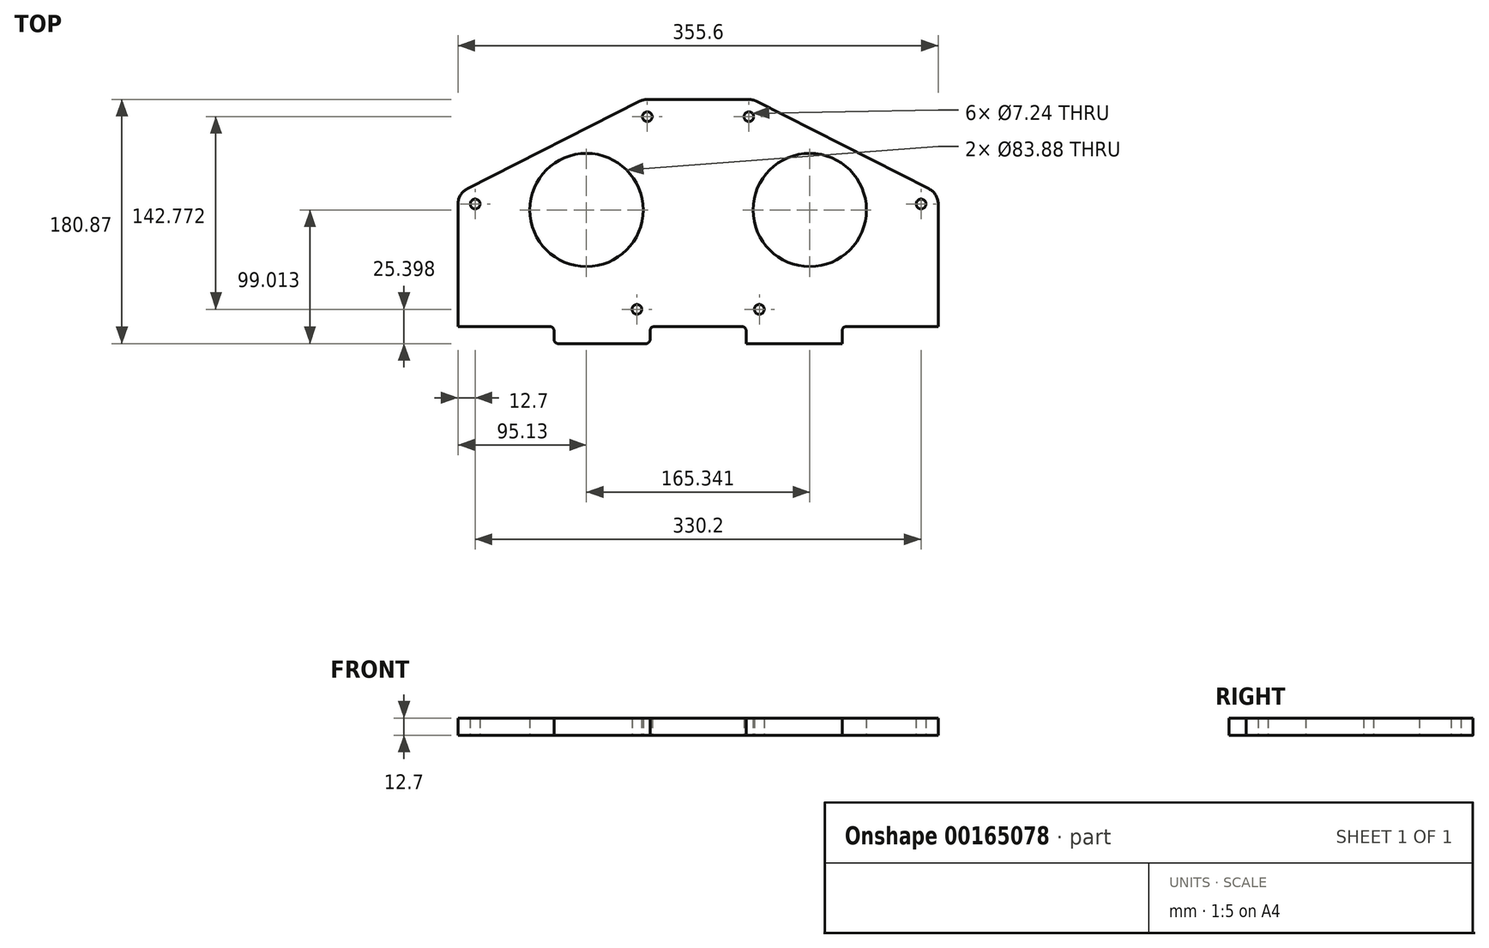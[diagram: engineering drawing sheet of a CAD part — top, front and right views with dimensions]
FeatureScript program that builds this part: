
annotation { "Feature Type Name" : "Feature", "Feature Type Description" : "" }
export const myFeature = defineFeature(function(context is Context, id is Id, definition is map)
    precondition{}
    {
        {
            var Q0;
            Q0=qCreatedBy(makeId("Top.planeOp"),FACE);
            var sketch = newSketch(context, id + "F0", { "sketchPlane" : qUnion([Q0])});
            skLineSegment(sketch, "E0.bottom", {"start": v(-37.6, 0) * mm, "end": v(37.6, 0) * mm});
            skLineSegment(sketch, "E0.top", {"start": v(-177.8, -180.87) * mm, "end": v(177.8, -180.87) * mm});
            skLineSegment(sketch, "E0.left", {"start": v(-177.8, -77.4) * mm, "end": v(-177.8, -180.87) * mm});
            skLineSegment(sketch, "E0.right", {"start": v(177.8, -77.4) * mm, "end": v(177.8, -180.87) * mm});
            skLineSegment(sketch, "E1", {"start": v(-177.8, -81.86) * mm, "end": v(-82.67, -81.86) * mm, "construction": true});
            skLineSegment(sketch, "E2", {"start": v(-82.67, -81.86) * mm, "end": v(-82.67, 0) * mm, "construction": true});
            skLineSegment(sketch, "E3", {"start": v(177.8, -81.86) * mm, "end": v(82.67, -81.86) * mm, "construction": true});
            skLineSegment(sketch, "E4", {"start": v(82.67, -81.86) * mm, "end": v(82.67, 0) * mm, "construction": true});
            skCircle(sketch, "E5", {"center": v(-82.67, -81.86) * mm, "radius": 41.94 * mm});
            skCircle(sketch, "E6", {"center": v(82.67, -81.86) * mm, "radius": 41.94 * mm});
            skLineSegment(sketch, "E7", {"start": v(-82.67, -81.86) * mm, "end": v(-45.32, -155.47) * mm, "construction": true});
            skLineSegment(sketch, "E8", {"start": v(-45.32, -155.47) * mm, "end": v(-165.1, -77.4) * mm, "construction": true});
            skLineSegment(sketch, "E9", {"start": v(-165.1, -77.4) * mm, "end": v(-82.67, -81.86) * mm, "construction": true});
            skLineSegment(sketch, "E10", {"start": v(-82.67, -81.86) * mm, "end": v(-37.6, -12.7) * mm, "construction": true});
            skLineSegment(sketch, "E11", {"start": v(-37.6, -12.7) * mm, "end": v(-165.1, -77.4) * mm, "construction": true});
            skLineSegment(sketch, "E12", {"start": v(-45.32, -155.47) * mm, "end": v(-37.6, -12.7) * mm, "construction": true});
            skLineSegment(sketch, "E13", {"start": v(82.67, -81.86) * mm, "end": v(165.1, -77.4) * mm, "construction": true});
            skLineSegment(sketch, "E14", {"start": v(165.1, -77.4) * mm, "end": v(45.32, -155.47) * mm, "construction": true});
            skLineSegment(sketch, "E15", {"start": v(45.32, -155.47) * mm, "end": v(82.67, -81.86) * mm, "construction": true});
            skLineSegment(sketch, "E16", {"start": v(82.67, -81.86) * mm, "end": v(37.6, -12.7) * mm, "construction": true});
            skLineSegment(sketch, "E17", {"start": v(37.6, -12.7) * mm, "end": v(45.32, -155.47) * mm, "construction": true});
            skLineSegment(sketch, "E18", {"start": v(37.6, -12.7) * mm, "end": v(165.1, -77.4) * mm, "construction": true});
            skCircle(sketch, "E19", {"center": v(-45.32, -155.47) * mm, "radius": 3.62 * mm});
            skCircle(sketch, "E20", {"center": v(-37.6, -12.7) * mm, "radius": 3.62 * mm});
            skCircle(sketch, "E21", {"center": v(-165.1, -77.4) * mm, "radius": 3.62 * mm});
            skCircle(sketch, "E22", {"center": v(45.32, -155.47) * mm, "radius": 3.62 * mm});
            skCircle(sketch, "E23", {"center": v(165.1, -77.4) * mm, "radius": 3.62 * mm});
            skCircle(sketch, "E24", {"center": v(37.6, -12.7) * mm, "radius": 3.62 * mm});
            skLineSegment(sketch, "E25", {"start": v(45.32, -155.47) * mm, "end": v(-45.32, -155.47) * mm, "construction": true});
            skLineSegment(sketch, "E26", {"start": v(0, -155.47) * mm, "end": v(0, -180.87) * mm, "construction": true});
            skArc(sketch, "E27", {"start": v(43.34, -1.37) * mm, "mid": v(40.55, -0.35) * mm, "end": v(37.6, 0) * mm});
            skArc(sketch, "E28", {"start": v(177.8, -77.4) * mm, "mid": v(175.92, -70.75) * mm, "end": v(170.85, -66.07) * mm});
            skLineSegment(sketch, "E29", {"start": v(170.85, -66.07) * mm, "end": v(43.34, -1.37) * mm});
            skArc(sketch, "E30", {"start": v(-37.6, 0) * mm, "mid": v(-40.55, -0.35) * mm, "end": v(-43.34, -1.37) * mm});
            skArc(sketch, "E31", {"start": v(-170.85, -66.07) * mm, "mid": v(-175.92, -70.75) * mm, "end": v(-177.8, -77.4) * mm});
            skLineSegment(sketch, "E32", {"start": v(-43.34, -1.37) * mm, "end": v(-170.85, -66.07) * mm});
            skSolve(sketch);
        }
        {
            var Q0;
            Q0=makeQuery(id+"F0.imprint","IMPRINT",FACE,{"disambiguationData":[TD([[makeQuery(id+"F0.imprint","IMPRINT",EDGE,{"derivedFrom":sQuery(id+"F0.wireOp",EDGE,"E0.top")}),1.0]])]});
            extrude(context, id + "F1", {"entities" : qUnion([Q0]), "depth" : 12.7 * mm});
        }
        {
            var Q0;
            Q0=makeQuery(id+"F1.opExtrude","CAP_FACE",FACE,{"disambiguationData":[OSD([sQuery(id+"F0.wireOp",EDGE,"E0.bottom"),sQuery(id+"F0.wireOp",EDGE,"E0.top"),sQuery(id+"F0.wireOp",EDGE,"E0.left"),sQuery(id+"F0.wireOp",EDGE,"E0.right"),sQuery(id+"F0.wireOp",EDGE,"E5"),sQuery(id+"F0.wireOp",EDGE,"E6"),sQuery(id+"F0.wireOp",EDGE,"E19"),sQuery(id+"F0.wireOp",EDGE,"E20"),sQuery(id+"F0.wireOp",EDGE,"E21"),sQuery(id+"F0.wireOp",EDGE,"E22"),sQuery(id+"F0.wireOp",EDGE,"E23"),sQuery(id+"F0.wireOp",EDGE,"E24"),sQuery(id+"F0.wireOp",EDGE,"E27"),sQuery(id+"F0.wireOp",EDGE,"E28"),sQuery(id+"F0.wireOp",EDGE,"E29"),sQuery(id+"F0.wireOp",EDGE,"E30"),sQuery(id+"F0.wireOp",EDGE,"E31"),sQuery(id+"F0.wireOp",EDGE,"E32")])],"isStart":false});
            var sketch = newSketch(context, id + "F2", { "sketchPlane" : qUnion([Q0])});
            skLineSegment(sketch, "E33.bottom", {"start": v(-177.8, -180.87) * mm, "end": v(-106.68, -180.87) * mm});
            skLineSegment(sketch, "E33.top", {"start": v(-177.8, -168.17) * mm, "end": v(-106.68, -168.17) * mm});
            skLineSegment(sketch, "E33.left", {"start": v(-177.8, -180.87) * mm, "end": v(-177.8, -168.17) * mm});
            skLineSegment(sketch, "E33.right", {"start": v(-106.68, -180.87) * mm, "end": v(-106.68, -168.17) * mm});
            skLineSegment(sketch, "E34.bottom", {"start": v(106.68, -180.87) * mm, "end": v(177.8, -180.87) * mm});
            skLineSegment(sketch, "E34.top", {"start": v(106.68, -168.17) * mm, "end": v(177.8, -168.17) * mm});
            skLineSegment(sketch, "E34.left", {"start": v(106.68, -180.87) * mm, "end": v(106.68, -168.17) * mm});
            skLineSegment(sketch, "E34.right", {"start": v(177.8, -180.87) * mm, "end": v(177.8, -168.17) * mm});
            skLineSegment(sketch, "E35.bottom", {"start": v(-35.56, -180.87) * mm, "end": v(35.56, -180.87) * mm});
            skLineSegment(sketch, "E35.top", {"start": v(-35.56, -168.17) * mm, "end": v(35.56, -168.17) * mm});
            skLineSegment(sketch, "E35.left", {"start": v(-35.56, -180.87) * mm, "end": v(-35.56, -168.17) * mm});
            skLineSegment(sketch, "E35.right", {"start": v(35.56, -180.87) * mm, "end": v(35.56, -168.17) * mm});
            skLineSegment(sketch, "E36", {"start": v(-106.68, -168.17) * mm, "end": v(-35.56, -168.17) * mm, "construction": true});
            skLineSegment(sketch, "E37", {"start": v(106.68, -168.17) * mm, "end": v(35.56, -168.17) * mm, "construction": true});
            skSolve(sketch);
        }
        {
            var Q0;
            Q0 = qSketchRegion(id + "F2", true);
            var Q1;
            Q1=makeQuery(id+"F1.opExtrude","CAP_FACE",FACE,{"disambiguationData":[OSD([sQuery(id+"F0.wireOp",EDGE,"E0.bottom"),sQuery(id+"F0.wireOp",EDGE,"E0.top"),sQuery(id+"F0.wireOp",EDGE,"E0.left"),sQuery(id+"F0.wireOp",EDGE,"E0.right"),sQuery(id+"F0.wireOp",EDGE,"E5"),sQuery(id+"F0.wireOp",EDGE,"E6"),sQuery(id+"F0.wireOp",EDGE,"E19"),sQuery(id+"F0.wireOp",EDGE,"E20"),sQuery(id+"F0.wireOp",EDGE,"E21"),sQuery(id+"F0.wireOp",EDGE,"E22"),sQuery(id+"F0.wireOp",EDGE,"E23"),sQuery(id+"F0.wireOp",EDGE,"E24"),sQuery(id+"F0.wireOp",EDGE,"E27"),sQuery(id+"F0.wireOp",EDGE,"E28"),sQuery(id+"F0.wireOp",EDGE,"E29"),sQuery(id+"F0.wireOp",EDGE,"E30"),sQuery(id+"F0.wireOp",EDGE,"E31"),sQuery(id+"F0.wireOp",EDGE,"E32")])],"isStart":true});
            extrude(context, id + "F3", {"entities" : qUnion([Q0]), "operationType" : NewBodyOperationType.REMOVE, "endBound" : BoundingType.UP_TO_SURFACE, "oppositeDirection" : true, "endBoundEntityFace" : qUnion([Q1]), "depth" : 25.4 * mm});
        }
        {
            var Q0;
            Q0=makeQuery(id+"F3.boolean.opBoolean","COPY",EDGE,{"derivedFrom":makeQuery(id+"F3.opExtrude","SWEPT_EDGE",EDGE,{"disambiguationData":[OSD([sQuery(id+"F0.wireOp",EDGE,"E0.left"),sQuery(id+"F2.wireOp",EDGE,"E33.top"),sQuery(id+"F2.wireOp",EDGE,"E33.left")])]})});
            var Q1;
            Q1=makeQuery(id+"F3.boolean.opBoolean","COPY",EDGE,{"derivedFrom":makeQuery(id+"F3.opExtrude","SWEPT_EDGE",EDGE,{"disambiguationData":[OSD([sQuery(id+"F2.wireOp",EDGE,"E33.top"),sQuery(id+"F2.wireOp",EDGE,"E33.right")])]})});
            var Q2;
            Q2=makeQuery(id+"F3.boolean.opBoolean","COPY",EDGE,{"derivedFrom":makeQuery(id+"F3.opExtrude","SWEPT_EDGE",EDGE,{"disambiguationData":[OSD([sQuery(id+"F2.wireOp",EDGE,"E35.top"),sQuery(id+"F2.wireOp",EDGE,"E35.left")])]})});
            var Q3;
            Q3=makeQuery(id+"F3.boolean.opBoolean","COPY",EDGE,{"derivedFrom":makeQuery(id+"F3.opExtrude","SWEPT_EDGE",EDGE,{"disambiguationData":[OSD([sQuery(id+"F2.wireOp",EDGE,"E35.top"),sQuery(id+"F2.wireOp",EDGE,"E35.right")])]})});
            var Q4;
            Q4=makeQuery(id+"F3.boolean.opBoolean","COPY",EDGE,{"derivedFrom":makeQuery(id+"F3.opExtrude","SWEPT_EDGE",EDGE,{"disambiguationData":[OSD([sQuery(id+"F2.wireOp",EDGE,"E34.top"),sQuery(id+"F2.wireOp",EDGE,"E34.left")])]})});
            var Q5;
            Q5=makeQuery(id+"F3.boolean.opBoolean","COPY",EDGE,{"derivedFrom":makeQuery(id+"F3.opExtrude","SWEPT_EDGE",EDGE,{"disambiguationData":[OSD([sQuery(id+"F0.wireOp",EDGE,"E0.right"),sQuery(id+"F2.wireOp",EDGE,"E34.top"),sQuery(id+"F2.wireOp",EDGE,"E34.right")])]})});
            var Q6;
            Q6=makeQuery(id+"F1.opExtrude","SWEPT_EDGE",EDGE,{"disambiguationData":[OSD([sQuery(id+"F0.wireOp",EDGE,"E0.top"),sQuery(id+"F0.wireOp",EDGE,"E0.left")])]});
            var Q7;
            Q7=makeQuery(id+"F3.boolean.opBoolean","COPY",EDGE,{"derivedFrom":makeQuery(id+"F3.opExtrude","SWEPT_EDGE",EDGE,{"disambiguationData":[OSD([sQuery(id+"F0.wireOp",EDGE,"E0.top"),sQuery(id+"F2.wireOp",EDGE,"E33.bottom"),sQuery(id+"F2.wireOp",EDGE,"E33.left")])]})});
            var Q8;
            Q8=makeQuery(id+"F3.boolean.opBoolean","COPY",EDGE,{"derivedFrom":makeQuery(id+"F3.opExtrude","SWEPT_EDGE",EDGE,{"disambiguationData":[OSD([sQuery(id+"F0.wireOp",EDGE,"E0.top"),sQuery(id+"F2.wireOp",EDGE,"E33.bottom"),sQuery(id+"F2.wireOp",EDGE,"E33.right")])]})});
            var Q9;
            Q9=makeQuery(id+"F3.boolean.opBoolean","COPY",EDGE,{"derivedFrom":makeQuery(id+"F3.opExtrude","SWEPT_EDGE",EDGE,{"disambiguationData":[OSD([sQuery(id+"F0.wireOp",EDGE,"E0.top"),sQuery(id+"F2.wireOp",EDGE,"E35.bottom"),sQuery(id+"F2.wireOp",EDGE,"E35.left")])]})});
            var Q10;
            Q10=makeQuery(id+"F3.boolean.opBoolean","COPY",EDGE,{"derivedFrom":makeQuery(id+"F3.opExtrude","SWEPT_EDGE",EDGE,{"disambiguationData":[OSD([sQuery(id+"F0.wireOp",EDGE,"E0.top"),sQuery(id+"F2.wireOp",EDGE,"E35.bottom"),sQuery(id+"F2.wireOp",EDGE,"E35.right")])]})});
            var Q11;
            Q11=makeQuery(id+"F3.boolean.opBoolean","COPY",EDGE,{"derivedFrom":makeQuery(id+"F3.opExtrude","SWEPT_EDGE",EDGE,{"disambiguationData":[OSD([sQuery(id+"F0.wireOp",EDGE,"E0.top"),sQuery(id+"F2.wireOp",EDGE,"E34.bottom"),sQuery(id+"F2.wireOp",EDGE,"E34.left")])]})});
            var Q12;
            Q12=makeQuery(id+"F3.boolean.opBoolean","COPY",EDGE,{"derivedFrom":makeQuery(id+"F3.opExtrude","SWEPT_EDGE",EDGE,{"disambiguationData":[OSD([sQuery(id+"F0.wireOp",EDGE,"E0.top"),sQuery(id+"F2.wireOp",EDGE,"E34.bottom"),sQuery(id+"F2.wireOp",EDGE,"E34.right")])]})});
            var Q13;
            Q13=makeQuery(id+"F1.opExtrude","SWEPT_EDGE",EDGE,{"disambiguationData":[OSD([sQuery(id+"F0.wireOp",EDGE,"E0.top"),sQuery(id+"F0.wireOp",EDGE,"E0.right")])]});
            fillet(context, id + "F4", {"entities" : qUnion([Q0, Q1, Q2, Q3, Q4, Q5, Q6, Q7, Q8, Q9, Q10, Q11, Q12, Q13]), "radius" : 3.17 * mm, "tangentPropagation" : true, "allowEdgeOverflow" : false});
        }
    });
